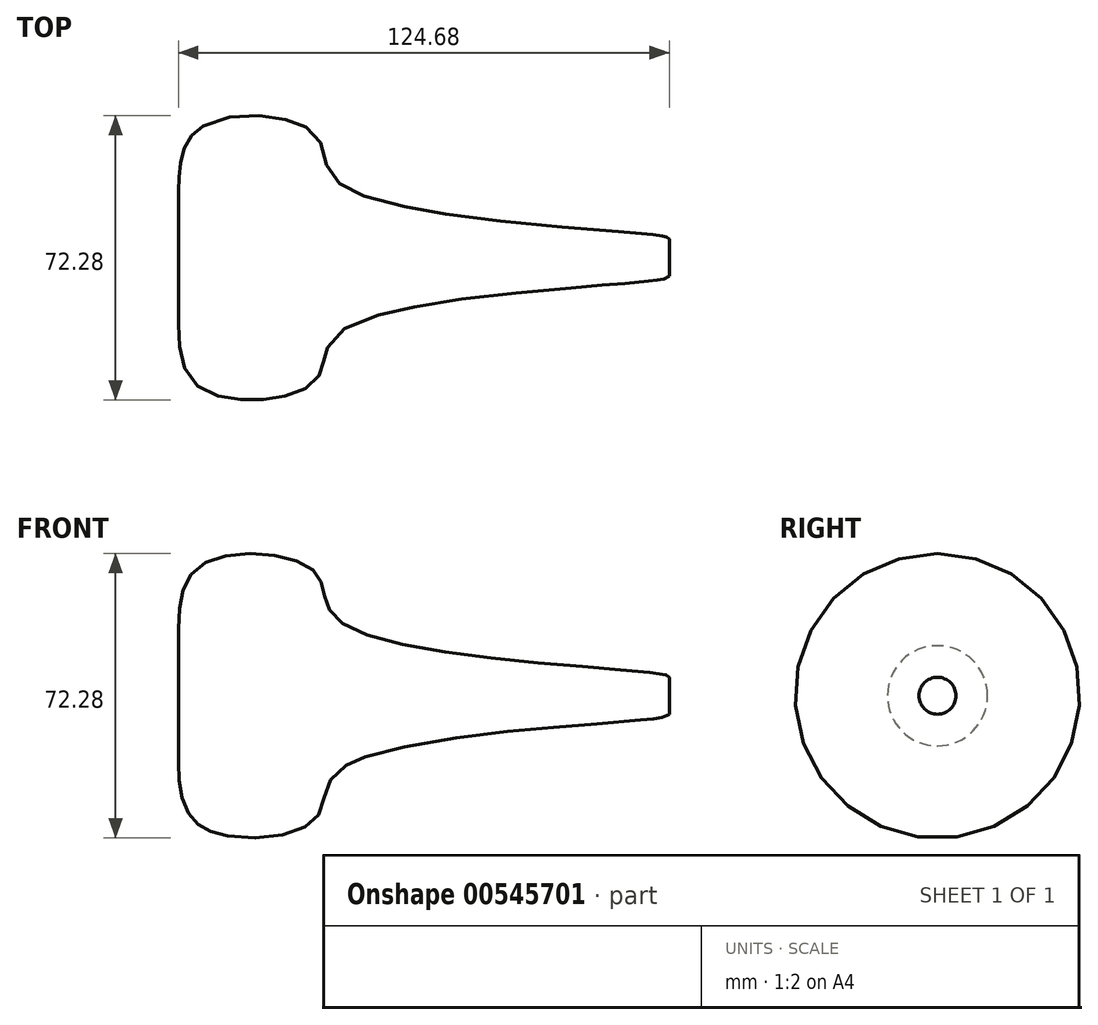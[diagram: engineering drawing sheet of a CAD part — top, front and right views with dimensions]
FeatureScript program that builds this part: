
annotation { "Feature Type Name" : "Feature", "Feature Type Description" : "" }
export const myFeature = defineFeature(function(context is Context, id is Id, definition is map)
    precondition{}
    {
        {
            var Q0;
            Q0=qCreatedBy(makeId("Front.planeOp"),FACE);
            var sketch = newSketch(context, id + "F0", { "sketchPlane" : qUnion([Q0])});
            skFitSpline(sketch, "E0", {"points": [v(-59.68, 12.71) * mm, v(-53.6, 33.43) * mm, v(-25.14, 31.5) * mm, v(-17.96, 18.24) * mm, v(64.38, 5.25) * mm, v(64.93, 4.7) * mm], "startDerivative": vector(-2.92, 129.58) * mm, "endDerivative": vector(0.56, -15.02) * mm});
            skLineSegment(sketch, "E1", {"start": v(-59.68, 12.71) * mm, "end": v(-59.68, 0) * mm});
            skLineSegment(sketch, "E2", {"start": v(64.93, 4.7) * mm, "end": v(64.93, 0) * mm});
            skLineSegment(sketch, "E3", {"start": v(-59.68, 0) * mm, "end": v(64.93, 0) * mm});
            skSolve(sketch);
        }
        {
            var Q0;
            Q0 = qSketchRegion(id + "F0", true);
            var Q1;
            Q1=sQuery(id+"F0.wireOp",EDGE,"E3");
            var Q2;
            Q2=sQuery(id+"F0.wireOp",EDGE,"E3");
            revolve(context, id + "F1", {"entities" : qUnion([Q0]), "axis" : qUnion([Q1, Q2]), "revolveType" : RevolveType.FULL});
        }
    });
